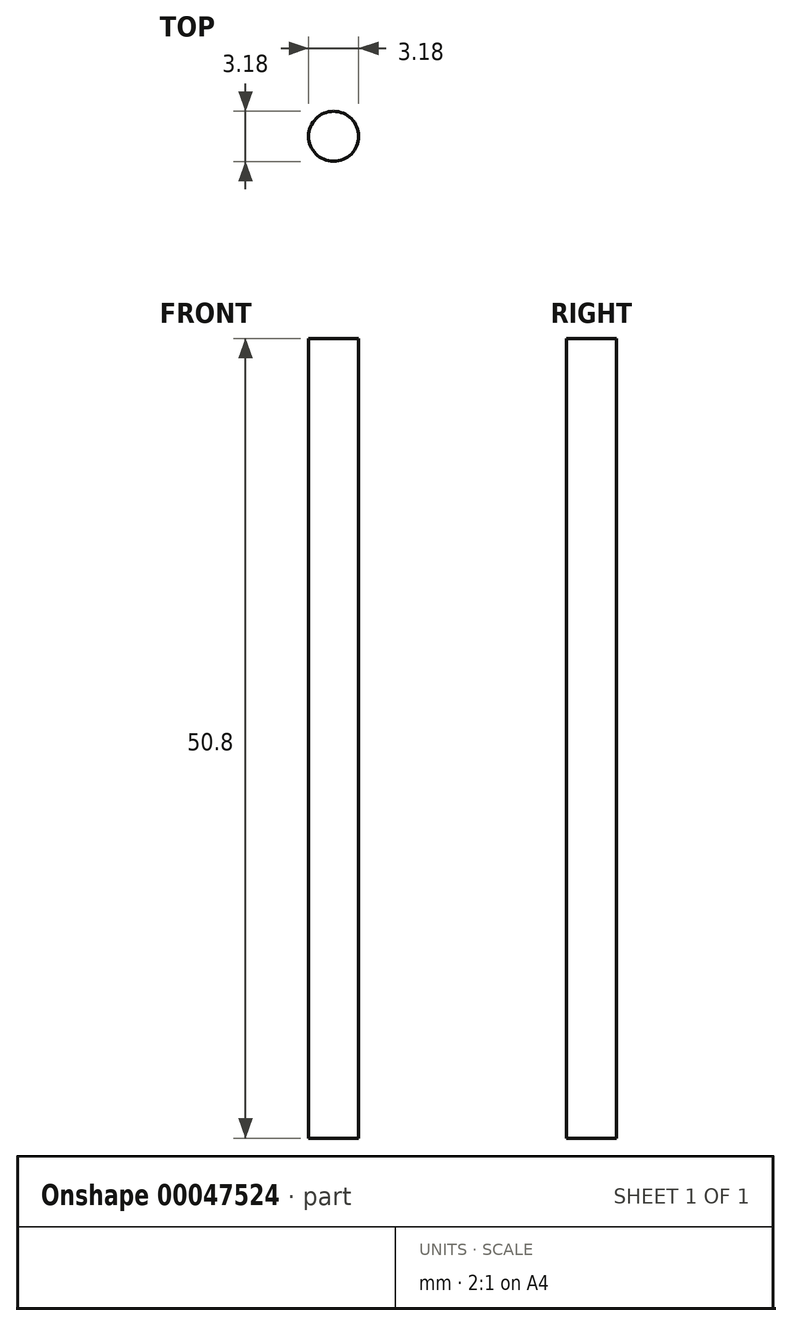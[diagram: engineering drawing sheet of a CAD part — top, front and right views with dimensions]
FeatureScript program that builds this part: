
annotation { "Feature Type Name" : "Feature", "Feature Type Description" : "" }
export const myFeature = defineFeature(function(context is Context, id is Id, definition is map)
    precondition{}
    {
        {
            var Q0;
            Q0=qCreatedBy(makeId("Top.planeOp"),FACE);
            var sketch = newSketch(context, id + "F0", { "sketchPlane" : qUnion([Q0])});
            skCircle(sketch, "E0", {"center": v(0, 0) * mm, "radius": 1.59 * mm});
            skSolve(sketch);
        }
        {
            var Q0;
            Q0 = qSketchRegion(id + "F0", true);
            extrude(context, id + "F1", {"entities" : qUnion([Q0]), "endBound" : BoundingType.SYMMETRIC, "depth" : 50.8 * mm});
        }
    });
